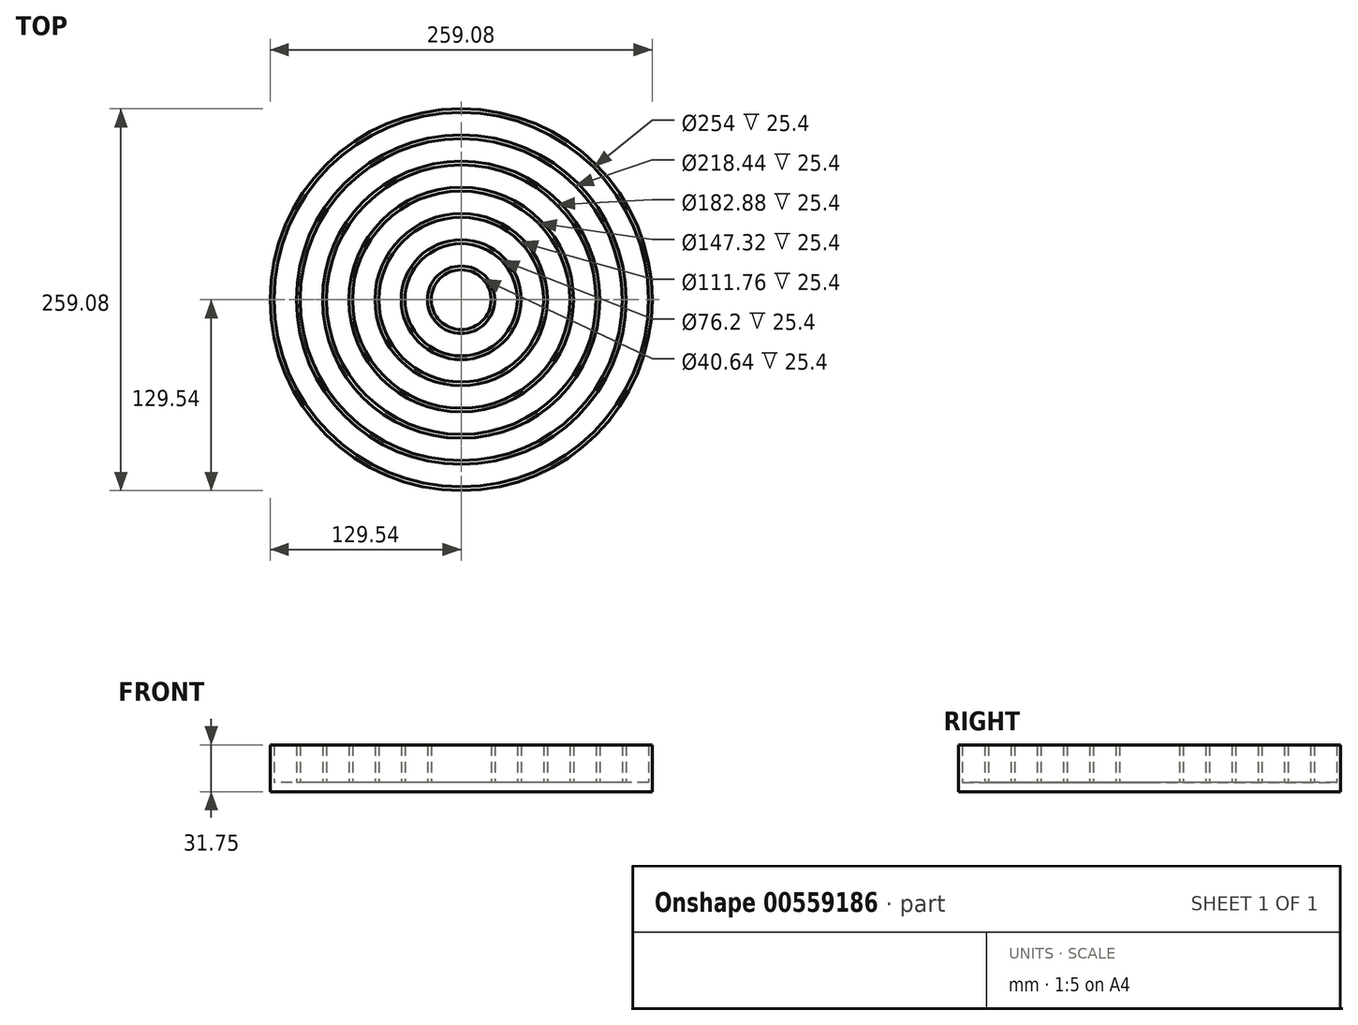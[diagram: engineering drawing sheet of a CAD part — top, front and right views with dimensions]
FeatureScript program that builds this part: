
annotation { "Feature Type Name" : "Feature", "Feature Type Description" : "" }
export const myFeature = defineFeature(function(context is Context, id is Id, definition is map)
    precondition{}
    {
        {
            var Q0;
            Q0=qCreatedBy(makeId("Top.planeOp"),FACE);
            var sketch = newSketch(context, id + "F0", { "sketchPlane" : qUnion([Q0])});
            skCircle(sketch, "E0", {"center": v(0, 0) * mm, "radius": 127 * mm});
            skCircle(sketch, "E1", {"center": v(0, 0) * mm, "radius": 109.22 * mm});
            skCircle(sketch, "E2", {"center": v(0, 0) * mm, "radius": 91.44 * mm});
            skCircle(sketch, "E3", {"center": v(0, 0) * mm, "radius": 73.66 * mm});
            skCircle(sketch, "E4", {"center": v(0, 0) * mm, "radius": 55.88 * mm});
            skCircle(sketch, "E5", {"center": v(0, 0) * mm, "radius": 38.1 * mm});
            skCircle(sketch, "E6", {"center": v(0, 0) * mm, "radius": 20.32 * mm});
            skLineSegment(sketch, "E7", {"start": v(-55.88, 0) * mm, "end": v(-73.66, 0) * mm});
            skLineSegment(sketch, "E8", {"start": v(-73.66, 0) * mm, "end": v(-91.44, 0) * mm});
            skLineSegment(sketch, "E9", {"start": v(-91.44, 0) * mm, "end": v(-109.22, 0) * mm});
            skLineSegment(sketch, "E10", {"start": v(-109.22, 0) * mm, "end": v(-127, 0) * mm});
            skCircle(sketch, "E11", {"center": v(-118.11, 0) * mm, "radius": 6.35 * mm});
            skPoint(sketch, "E12", {"position": v(-124.46, 0) * mm});
            skLineSegment(sketch, "E13", {"start": v(-55.88, 0) * mm, "end": v(-38.1, 0) * mm});
            skLineSegment(sketch, "E14", {"start": v(-38.1, 0) * mm, "end": v(-20.32, 0) * mm});
            skCircle(sketch, "E15", {"center": v(0, 0) * mm, "radius": 2.54 * mm});
            skLineSegment(sketch, "E16", {"start": v(-20.32, 0) * mm, "end": v(-2.54, 0) * mm});
            skSolve(sketch);
        }
        {
            var Q0;
            Q0=qCreatedBy(makeId("Top.planeOp"),FACE);
            var sketch = newSketch(context, id + "F1", { "sketchPlane" : qUnion([Q0])});
            skCircle(sketch, "E17.0", {"center": v(0, 0) * mm, "radius": 127 * mm, "construction": true});
            skCircle(sketch, "E18.0", {"center": v(0, 0) * mm, "radius": 129.54 * mm});
            skSolve(sketch);
        }
        {
            var Q0;
            Q0=qCreatedBy(makeId("Top.planeOp"),FACE);
            var sketch = newSketch(context, id + "F2", { "sketchPlane" : qUnion([Q0])});
            skCircle(sketch, "E19.0", {"center": v(0, 0) * mm, "radius": 129.54 * mm});
            skCircle(sketch, "E20.0", {"center": v(0, 0) * mm, "radius": 111.76 * mm});
            skCircle(sketch, "E21.0", {"center": v(0, 0) * mm, "radius": 93.98 * mm});
            skCircle(sketch, "E22.0", {"center": v(0, 0) * mm, "radius": 76.2 * mm});
            skCircle(sketch, "E23.0", {"center": v(0, 0) * mm, "radius": 58.42 * mm});
            skCircle(sketch, "E24.0", {"center": v(0, 0) * mm, "radius": 40.64 * mm});
            skCircle(sketch, "E25.0", {"center": v(0, 0) * mm, "radius": 22.86 * mm});
            skCircle(sketch, "E26.0", {"center": v(0, 0) * mm, "radius": 127 * mm});
            skCircle(sketch, "E27.0", {"center": v(0, 0) * mm, "radius": 109.22 * mm});
            skCircle(sketch, "E27.1", {"center": v(0, 0) * mm, "radius": 91.44 * mm});
            skCircle(sketch, "E27.2", {"center": v(0, 0) * mm, "radius": 73.66 * mm});
            skCircle(sketch, "E27.3", {"center": v(0, 0) * mm, "radius": 55.88 * mm});
            skCircle(sketch, "E27.4", {"center": v(0, 0) * mm, "radius": 38.1 * mm});
            skCircle(sketch, "E27.5", {"center": v(0, 0) * mm, "radius": 20.32 * mm});
            skSolve(sketch);
        }
        {
            var Q0;
            Q0 = qSketchRegion(id + "F1", true);
            extrude(context, id + "F3", {"entities" : qUnion([Q0]), "oppositeDirection" : true, "depth" : 6.35 * mm, "offsetDistance" : 25.4 * mm});
        }
        {
            var Q0;
            Q0=makeQuery(id+"F2.imprint","IMPRINT",FACE,{"disambiguationData":[TD([[makeQuery(id+"F2.imprint","IMPRINT",EDGE,{"derivedFrom":sQuery(id+"F2.wireOp",EDGE,"E19.0")}),1.0]])]});
            var Q1;
            Q1=makeQuery(id+"F2.imprint","IMPRINT",FACE,{"disambiguationData":[TD([[makeQuery(id+"F2.imprint","IMPRINT",EDGE,{"derivedFrom":sQuery(id+"F2.wireOp",EDGE,"E20.0")}),1.0]])]});
            var Q2;
            Q2=makeQuery(id+"F2.imprint","IMPRINT",FACE,{"disambiguationData":[TD([[makeQuery(id+"F2.imprint","IMPRINT",EDGE,{"derivedFrom":sQuery(id+"F2.wireOp",EDGE,"E21.0")}),1.0]])]});
            var Q3;
            Q3=makeQuery(id+"F2.imprint","IMPRINT",FACE,{"disambiguationData":[TD([[makeQuery(id+"F2.imprint","IMPRINT",EDGE,{"derivedFrom":sQuery(id+"F2.wireOp",EDGE,"E22.0")}),1.0]])]});
            var Q4;
            Q4=makeQuery(id+"F2.imprint","IMPRINT",FACE,{"disambiguationData":[TD([[makeQuery(id+"F2.imprint","IMPRINT",EDGE,{"derivedFrom":sQuery(id+"F2.wireOp",EDGE,"E23.0")}),1.0]])]});
            var Q5;
            Q5=makeQuery(id+"F2.imprint","IMPRINT",FACE,{"disambiguationData":[TD([[makeQuery(id+"F2.imprint","IMPRINT",EDGE,{"derivedFrom":sQuery(id+"F2.wireOp",EDGE,"E24.0")}),1.0]])]});
            var Q6;
            Q6=makeQuery(id+"F2.imprint","IMPRINT",FACE,{"disambiguationData":[TD([[makeQuery(id+"F2.imprint","IMPRINT",EDGE,{"derivedFrom":sQuery(id+"F2.wireOp",EDGE,"E25.0")}),1.0]])]});
            extrude(context, id + "F4", {"entities" : qUnion([Q0, Q1, Q2, Q3, Q4, Q5, Q6]), "operationType" : NewBodyOperationType.ADD, "depth" : 25.4 * mm, "offsetDistance" : 25.4 * mm});
        }
    });
